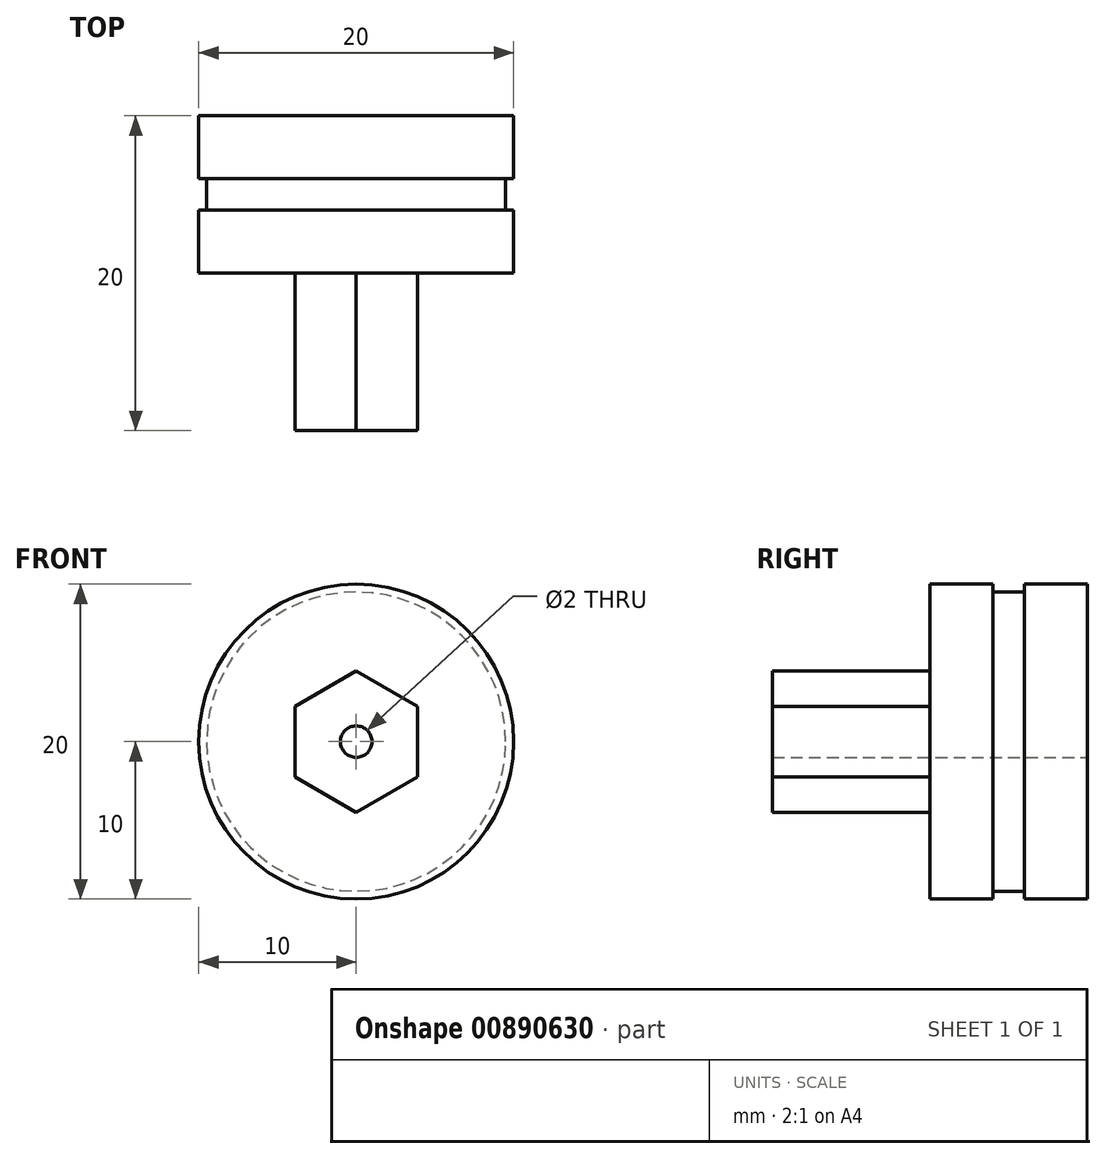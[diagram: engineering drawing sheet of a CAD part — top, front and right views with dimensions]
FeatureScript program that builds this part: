
annotation { "Feature Type Name" : "Feature", "Feature Type Description" : "" }
export const myFeature = defineFeature(function(context is Context, id is Id, definition is map)
    precondition{}
    {
        {
            var Q0;
            Q0=qCreatedBy(makeId("Front.planeOp"),FACE);
            var sketch = newSketch(context, id + "F0", { "sketchPlane" : qUnion([Q0])});
            skCircle(sketch, "E0", {"center": v(0, 0) * mm, "radius": 10 * mm});
            skCircle(sketch, "E1", {"center": v(0, 0) * mm, "radius": 4.5 * mm});
            skCircle(sketch, "E2", {"center": v(0, 0) * mm, "radius": 9.5 * mm});
            skCircle(sketch, "E3.cCircle", {"center": v(0, 0) * mm, "radius": 4.5 * mm, "construction": true});
            skLineSegment(sketch, "E3.0", {"start": v(0, 4.5) * mm, "end": v(3.9, 2.25) * mm});
            skLineSegment(sketch, "E3.1", {"start": v(3.9, 2.25) * mm, "end": v(3.9, -2.25) * mm});
            skLineSegment(sketch, "E3.2", {"start": v(3.9, -2.25) * mm, "end": v(0, -4.5) * mm});
            skLineSegment(sketch, "E3.3", {"start": v(0, -4.5) * mm, "end": v(-3.9, -2.25) * mm});
            skLineSegment(sketch, "E3.4", {"start": v(-3.9, -2.25) * mm, "end": v(-3.9, 2.25) * mm});
            skLineSegment(sketch, "E3.5", {"start": v(-3.9, 2.25) * mm, "end": v(0, 4.5) * mm});
            skCircle(sketch, "E4", {"center": v(0, 0) * mm, "radius": 1 * mm});
            skSolve(sketch);
        }
        {
            var Q0;
            Q0=makeQuery(id+"F0.imprint","IMPRINT",FACE,{"disambiguationData":[TD([[makeQuery(id+"F0.imprint","IMPRINT",EDGE,{"derivedFrom":sQuery(id+"F0.wireOp",EDGE,"E0")}),1.0]])]});
            var Q1;
            Q1=makeQuery(id+"F0.imprint","IMPRINT",FACE,{"disambiguationData":[TD([[makeQuery(id+"F0.imprint","IMPRINT",EDGE,{"derivedFrom":sQuery(id+"F0.wireOp",EDGE,"E2")}),1.0]])]});
            var Q2;
            {var subQ0=sQuery(id+"F0.wireOp",EDGE,"E3.0");Q2=makeQuery(id+"F0.imprint","IMPRINT",FACE,{"disambiguationData":[TD([[makeQuery(id+"F0.imprint","IMPRINT",EDGE,{"derivedFrom":subQ0}),1.0]])]});}
            var Q3;
            {var subQ0=sQuery(id+"F0.wireOp",EDGE,"E3.5");Q3=makeQuery(id+"F0.imprint","IMPRINT",FACE,{"disambiguationData":[TD([[makeQuery(id+"F0.imprint","IMPRINT",EDGE,{"derivedFrom":subQ0}),1.0]])]});}
            var Q4;
            {var subQ0=sQuery(id+"F0.wireOp",EDGE,"E3.4");Q4=makeQuery(id+"F0.imprint","IMPRINT",FACE,{"disambiguationData":[TD([[makeQuery(id+"F0.imprint","IMPRINT",EDGE,{"derivedFrom":subQ0}),1.0]])]});}
            var Q5;
            {var subQ0=sQuery(id+"F0.wireOp",EDGE,"E3.3");Q5=makeQuery(id+"F0.imprint","IMPRINT",FACE,{"disambiguationData":[TD([[makeQuery(id+"F0.imprint","IMPRINT",EDGE,{"derivedFrom":subQ0}),1.0]])]});}
            var Q6;
            {var subQ0=sQuery(id+"F0.wireOp",EDGE,"E3.2");Q6=makeQuery(id+"F0.imprint","IMPRINT",FACE,{"disambiguationData":[TD([[makeQuery(id+"F0.imprint","IMPRINT",EDGE,{"derivedFrom":subQ0}),1.0]])]});}
            var Q7;
            Q7=makeQuery(id+"F0.imprint","IMPRINT",FACE,{"disambiguationData":[TD([[makeQuery(id+"F0.imprint","IMPRINT",EDGE,{"derivedFrom":sQuery(id+"F0.wireOp",EDGE,"E3.0")}),-1.0]])]});
            var Q8;
            {var subQ0=sQuery(id+"F0.wireOp",EDGE,"E3.1");Q8=makeQuery(id+"F0.imprint","IMPRINT",FACE,{"disambiguationData":[TD([[makeQuery(id+"F0.imprint","IMPRINT",EDGE,{"derivedFrom":subQ0}),1.0]])]});}
            extrude(context, id + "F1", {"entities" : qUnion([Q0, Q1, Q2, Q3, Q4, Q5, Q6, Q7, Q8]), "depth" : 4 * mm, "offsetDistance" : 25 * mm});
        }
        {
            var Q0;
            {var subQ0=sQuery(id+"F0.wireOp",EDGE,"E3.5");Q0=makeQuery(id+"F0.imprint","IMPRINT",FACE,{"disambiguationData":[TD([[makeQuery(id+"F0.imprint","IMPRINT",EDGE,{"derivedFrom":subQ0}),1.0]])]});}
            var Q1;
            {var subQ0=sQuery(id+"F0.wireOp",EDGE,"E3.0");Q1=makeQuery(id+"F0.imprint","IMPRINT",FACE,{"disambiguationData":[TD([[makeQuery(id+"F0.imprint","IMPRINT",EDGE,{"derivedFrom":subQ0}),1.0]])]});}
            var Q2;
            Q2=makeQuery(id+"F0.imprint","IMPRINT",FACE,{"disambiguationData":[TD([[makeQuery(id+"F0.imprint","IMPRINT",EDGE,{"derivedFrom":sQuery(id+"F0.wireOp",EDGE,"E3.0")}),-1.0]])]});
            var Q3;
            {var subQ0=sQuery(id+"F0.wireOp",EDGE,"E3.1");Q3=makeQuery(id+"F0.imprint","IMPRINT",FACE,{"disambiguationData":[TD([[makeQuery(id+"F0.imprint","IMPRINT",EDGE,{"derivedFrom":subQ0}),1.0]])]});}
            var Q4;
            {var subQ0=sQuery(id+"F0.wireOp",EDGE,"E3.4");Q4=makeQuery(id+"F0.imprint","IMPRINT",FACE,{"disambiguationData":[TD([[makeQuery(id+"F0.imprint","IMPRINT",EDGE,{"derivedFrom":subQ0}),1.0]])]});}
            var Q5;
            {var subQ0=sQuery(id+"F0.wireOp",EDGE,"E3.3");Q5=makeQuery(id+"F0.imprint","IMPRINT",FACE,{"disambiguationData":[TD([[makeQuery(id+"F0.imprint","IMPRINT",EDGE,{"derivedFrom":subQ0}),1.0]])]});}
            var Q6;
            {var subQ0=sQuery(id+"F0.wireOp",EDGE,"E3.2");Q6=makeQuery(id+"F0.imprint","IMPRINT",FACE,{"disambiguationData":[TD([[makeQuery(id+"F0.imprint","IMPRINT",EDGE,{"derivedFrom":subQ0}),1.0]])]});}
            var Q7;
            Q7=makeQuery(id+"F0.imprint","IMPRINT",FACE,{"disambiguationData":[TD([[makeQuery(id+"F0.imprint","IMPRINT",EDGE,{"derivedFrom":sQuery(id+"F0.wireOp",EDGE,"E2")}),1.0]])]});
            extrude(context, id + "F2", {"entities" : qUnion([Q0, Q1, Q2, Q3, Q4, Q5, Q6, Q7]), "operationType" : NewBodyOperationType.ADD, "depth" : 6 * mm, "offsetDistance" : 25 * mm});
        }
        {
            var Q0;
            Q0=makeQuery(id+"F2.opExtrude","CAP_FACE",FACE,{"disambiguationData":[OSD([sQuery(id+"F0.wireOp",EDGE,"E2")])],"isStart":false});
            var sketch = newSketch(context, id + "F3", { "sketchPlane" : qUnion([Q0])});
            skCircle(sketch, "E5.0", {"center": v(0, 0) * mm, "radius": 10 * mm});
            skCircle(sketch, "E5.1", {"center": v(0, 0) * mm, "radius": 9.5 * mm});
            skCircle(sketch, "E5.2", {"center": v(0, 0) * mm, "radius": 4.5 * mm});
            skLineSegment(sketch, "E5.3", {"start": v(0, 4.5) * mm, "end": v(3.9, 2.25) * mm});
            skLineSegment(sketch, "E5.4", {"start": v(-3.9, 2.25) * mm, "end": v(0, 4.5) * mm});
            skLineSegment(sketch, "E5.5", {"start": v(0, -4.5) * mm, "end": v(-3.9, -2.25) * mm});
            skLineSegment(sketch, "E5.6", {"start": v(-3.9, -2.25) * mm, "end": v(-3.9, 2.25) * mm});
            skLineSegment(sketch, "E5.7", {"start": v(3.9, -2.25) * mm, "end": v(0, -4.5) * mm});
            skLineSegment(sketch, "E5.8", {"start": v(3.9, 2.25) * mm, "end": v(3.9, -2.25) * mm});
            skPoint(sketch, "E5.9", {"position": v(-1.95, 3.37) * mm});
            skPoint(sketch, "E5.10", {"position": v(1.95, 3.38) * mm});
            skPoint(sketch, "E5.11", {"position": v(-3.9, 0) * mm});
            skSolve(sketch);
        }
        {
            var Q0;
            Q0=makeQuery(id+"F3.imprint","IMPRINT",FACE,{"disambiguationData":[TD([[makeQuery(id+"F3.imprint","IMPRINT",EDGE,{"derivedFrom":sQuery(id+"F3.wireOp",EDGE,"E5.0")}),1.0]])]});
            var Q1;
            Q1=makeQuery(id+"F3.imprint","IMPRINT",FACE,{"disambiguationData":[TD([[makeQuery(id+"F3.imprint","IMPRINT",EDGE,{"derivedFrom":sQuery(id+"F3.wireOp",EDGE,"E5.1")}),1.0]])]});
            var Q2;
            {var subQ0=sQuery(id+"F3.wireOp",EDGE,"E5.4");Q2=makeQuery(id+"F3.imprint","IMPRINT",FACE,{"disambiguationData":[TD([[makeQuery(id+"F3.imprint","IMPRINT",EDGE,{"derivedFrom":subQ0}),1.0]])]});}
            var Q3;
            {var subQ0=sQuery(id+"F3.wireOp",EDGE,"E5.6");Q3=makeQuery(id+"F3.imprint","IMPRINT",FACE,{"disambiguationData":[TD([[makeQuery(id+"F3.imprint","IMPRINT",EDGE,{"derivedFrom":subQ0}),1.0]])]});}
            var Q4;
            {var subQ0=sQuery(id+"F3.wireOp",EDGE,"E5.3");Q4=makeQuery(id+"F3.imprint","IMPRINT",FACE,{"disambiguationData":[TD([[makeQuery(id+"F3.imprint","IMPRINT",EDGE,{"derivedFrom":subQ0}),1.0]])]});}
            var Q5;
            Q5=makeQuery(id+"F3.imprint","IMPRINT",FACE,{"disambiguationData":[TD([[makeQuery(id+"F3.imprint","IMPRINT",EDGE,{"derivedFrom":sQuery(id+"F3.wireOp",EDGE,"E5.3")}),-1.0]])]});
            var Q6;
            {var subQ0=sQuery(id+"F3.wireOp",EDGE,"E5.8");Q6=makeQuery(id+"F3.imprint","IMPRINT",FACE,{"disambiguationData":[TD([[makeQuery(id+"F3.imprint","IMPRINT",EDGE,{"derivedFrom":subQ0}),1.0]])]});}
            var Q7;
            {var subQ0=sQuery(id+"F3.wireOp",EDGE,"E5.7");Q7=makeQuery(id+"F3.imprint","IMPRINT",FACE,{"disambiguationData":[TD([[makeQuery(id+"F3.imprint","IMPRINT",EDGE,{"derivedFrom":subQ0}),1.0]])]});}
            var Q8;
            {var subQ0=sQuery(id+"F3.wireOp",EDGE,"E5.5");Q8=makeQuery(id+"F3.imprint","IMPRINT",FACE,{"disambiguationData":[TD([[makeQuery(id+"F3.imprint","IMPRINT",EDGE,{"derivedFrom":subQ0}),1.0]])]});}
            extrude(context, id + "F4", {"entities" : qUnion([Q0, Q1, Q2, Q3, Q4, Q5, Q6, Q7, Q8]), "depth" : 4 * mm, "offsetDistance" : 25 * mm});
        }
        {
            var Q0;
            Q0=makeQuery(id+"F3.imprint","IMPRINT",FACE,{"disambiguationData":[TD([[makeQuery(id+"F3.imprint","IMPRINT",EDGE,{"derivedFrom":sQuery(id+"F3.wireOp",EDGE,"E5.3")}),-1.0]])]});
            extrude(context, id + "F5", {"entities" : qUnion([Q0]), "operationType" : NewBodyOperationType.ADD, "depth" : 14 * mm, "offsetDistance" : 25 * mm});
        }
        {
            var Q0;
            Q0=makeQuery(id+"F3.imprint","IMPRINT",FACE,{"disambiguationData":[TD([[makeQuery(id+"F3.imprint","IMPRINT",EDGE,{"derivedFrom":makeQuery(id+"F2.opExtrude","CAP_EDGE",EDGE,{"disambiguationData":[OSD([sQuery(id+"F0.wireOp",EDGE,"E4")])],"isStart":false})}),1.0]])]});
            extrude(context, id + "F6", {"entities" : qUnion([Q0]), "operationType" : NewBodyOperationType.REMOVE, "depth" : 20 * mm, "offsetDistance" : 25 * mm});
        }
    });
